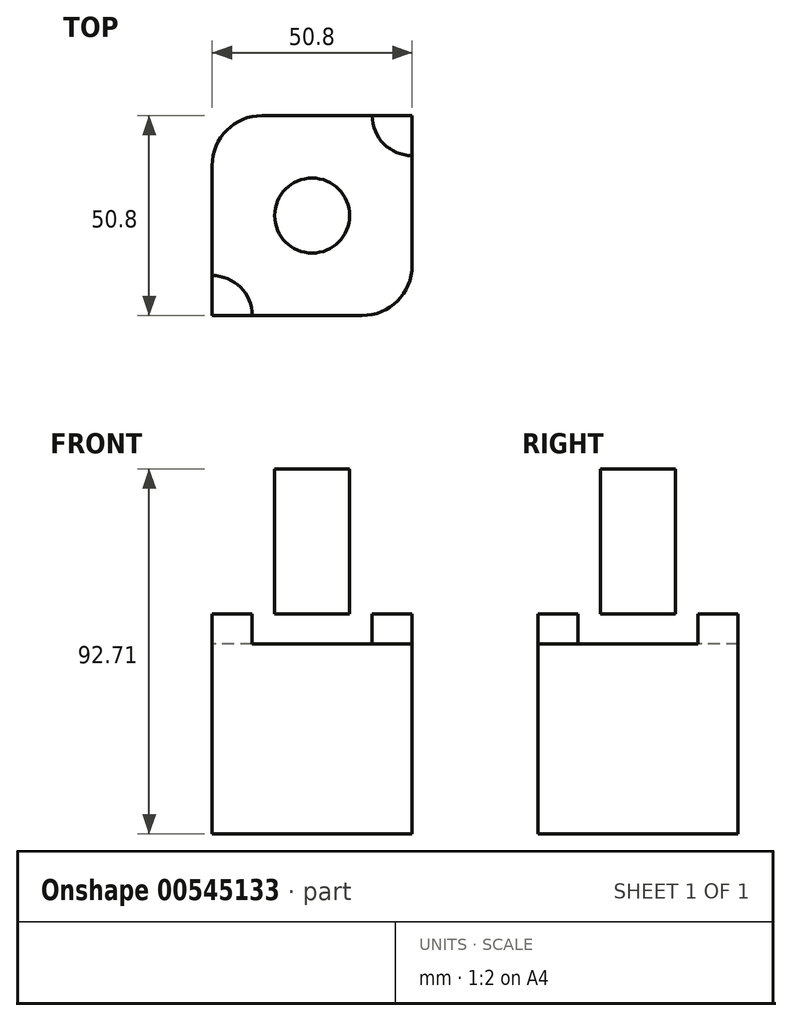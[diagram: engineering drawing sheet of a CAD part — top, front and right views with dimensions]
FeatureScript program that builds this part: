
annotation { "Feature Type Name" : "Feature", "Feature Type Description" : "" }
export const myFeature = defineFeature(function(context is Context, id is Id, definition is map)
    precondition{}
    {
        {
            var Q0;
            Q0=qCreatedBy(makeId("Top.planeOp"),FACE);
            var sketch = newSketch(context, id + "F0", { "sketchPlane" : qUnion([Q0])});
            skLineSegment(sketch, "E0.bottom", {"start": v(25.4, -25.4) * mm, "end": v(-25.4, -25.4) * mm});
            skLineSegment(sketch, "E0.top", {"start": v(25.4, 25.4) * mm, "end": v(-25.4, 25.4) * mm});
            skLineSegment(sketch, "E0.left", {"start": v(25.4, -25.4) * mm, "end": v(25.4, 25.4) * mm});
            skLineSegment(sketch, "E0.right", {"start": v(-25.4, -25.4) * mm, "end": v(-25.4, 25.4) * mm});
            skPoint(sketch, "E0.middle", {"position": v(0, 0) * mm});
            skSolve(sketch);
        }
        {
            var Q0;
            Q0=makeQuery(id+"F0.imprint","IMPRINT",FACE,{"disambiguationData":[TD([[makeQuery(id+"F0.imprint","IMPRINT",EDGE,{"derivedFrom":sQuery(id+"F0.wireOp",EDGE,"E0.bottom")}),-1.0]])]});
            extrude(context, id + "F1", {"entities" : qUnion([Q0]), "depth" : 55.88 * mm, "offsetDistance" : 25.4 * mm});
        }
        {
            var Q0;
            Q0=makeQuery(id+"F1.opExtrude","SWEPT_EDGE",EDGE,{"disambiguationData":[OSD([sQuery(id+"F0.wireOp",EDGE,"E0.top"),sQuery(id+"F0.wireOp",EDGE,"E0.right")])]});
            var Q1;
            Q1=makeQuery(id+"F1.opExtrude","SWEPT_EDGE",EDGE,{"disambiguationData":[OSD([sQuery(id+"F0.wireOp",EDGE,"E0.bottom"),sQuery(id+"F0.wireOp",EDGE,"E0.left")])]});
            fillet(context, id + "F2", {"entities" : qUnion([Q0, Q1]), "radius" : 12.7 * mm, "tangentPropagation" : true, "allowEdgeOverflow" : false});
        }
        {
            var Q0;
            Q0=makeQuery(id+"F1.opExtrude","CAP_FACE",FACE,{"disambiguationData":[OSD([sQuery(id+"F0.wireOp",EDGE,"E0.bottom"),sQuery(id+"F0.wireOp",EDGE,"E0.top"),sQuery(id+"F0.wireOp",EDGE,"E0.left"),sQuery(id+"F0.wireOp",EDGE,"E0.right")])],"isStart":false});
            var sketch = newSketch(context, id + "F3", { "sketchPlane" : qUnion([Q0])});
            skArc(sketch, "E1", {"start": v(-25.4, -15.24) * mm, "mid": v(-18.22, -18.22) * mm, "end": v(-15.24, -25.4) * mm});
            skArc(sketch, "E2", {"start": v(25.4, 15.24) * mm, "mid": v(18.22, 18.22) * mm, "end": v(15.24, 25.4) * mm});
            skSolve(sketch);
        }
        {
            var Q0;
            {var subQ0=sQuery(id+"F3.wireOp",EDGE,"E2");Q0=makeQuery(id+"F3.imprint","IMPRINT",FACE,{"disambiguationData":[TD([[makeQuery(id+"F3.imprint","IMPRINT",EDGE,{"derivedFrom":subQ0}),-1.0]])]});}
            var Q1;
            {var subQ0=sQuery(id+"F3.wireOp",EDGE,"E1");Q1=makeQuery(id+"F3.imprint","IMPRINT",FACE,{"disambiguationData":[TD([[makeQuery(id+"F3.imprint","IMPRINT",EDGE,{"derivedFrom":subQ0}),-1.0]])]});}
            extrude(context, id + "F4", {"entities" : qUnion([Q0, Q1]), "operationType" : NewBodyOperationType.REMOVE, "oppositeDirection" : true, "depth" : 7.62 * mm, "offsetDistance" : 25.4 * mm});
        }
        {
            var Q0;
            Q0=makeQuery(id+"F1.opExtrude","CAP_FACE",FACE,{"disambiguationData":[OSD([sQuery(id+"F0.wireOp",EDGE,"E0.bottom"),sQuery(id+"F0.wireOp",EDGE,"E0.top"),sQuery(id+"F0.wireOp",EDGE,"E0.left"),sQuery(id+"F0.wireOp",EDGE,"E0.right")])],"isStart":false});
            var sketch = newSketch(context, id + "F5", { "sketchPlane" : qUnion([Q0])});
            skCircle(sketch, "E3", {"center": v(0, 0) * mm, "radius": 9.53 * mm});
            skSolve(sketch);
        }
        {
            var Q0;
            Q0=makeQuery(id+"F5.imprint","IMPRINT",FACE,{"disambiguationData":[TD([[makeQuery(id+"F5.imprint","IMPRINT",EDGE,{"derivedFrom":sQuery(id+"F5.wireOp",EDGE,"E3")}),1.0]])]});
            extrude(context, id + "F6", {"entities" : qUnion([Q0]), "operationType" : NewBodyOperationType.ADD, "depth" : 36.83 * mm, "offsetDistance" : 25.4 * mm});
        }
    });
